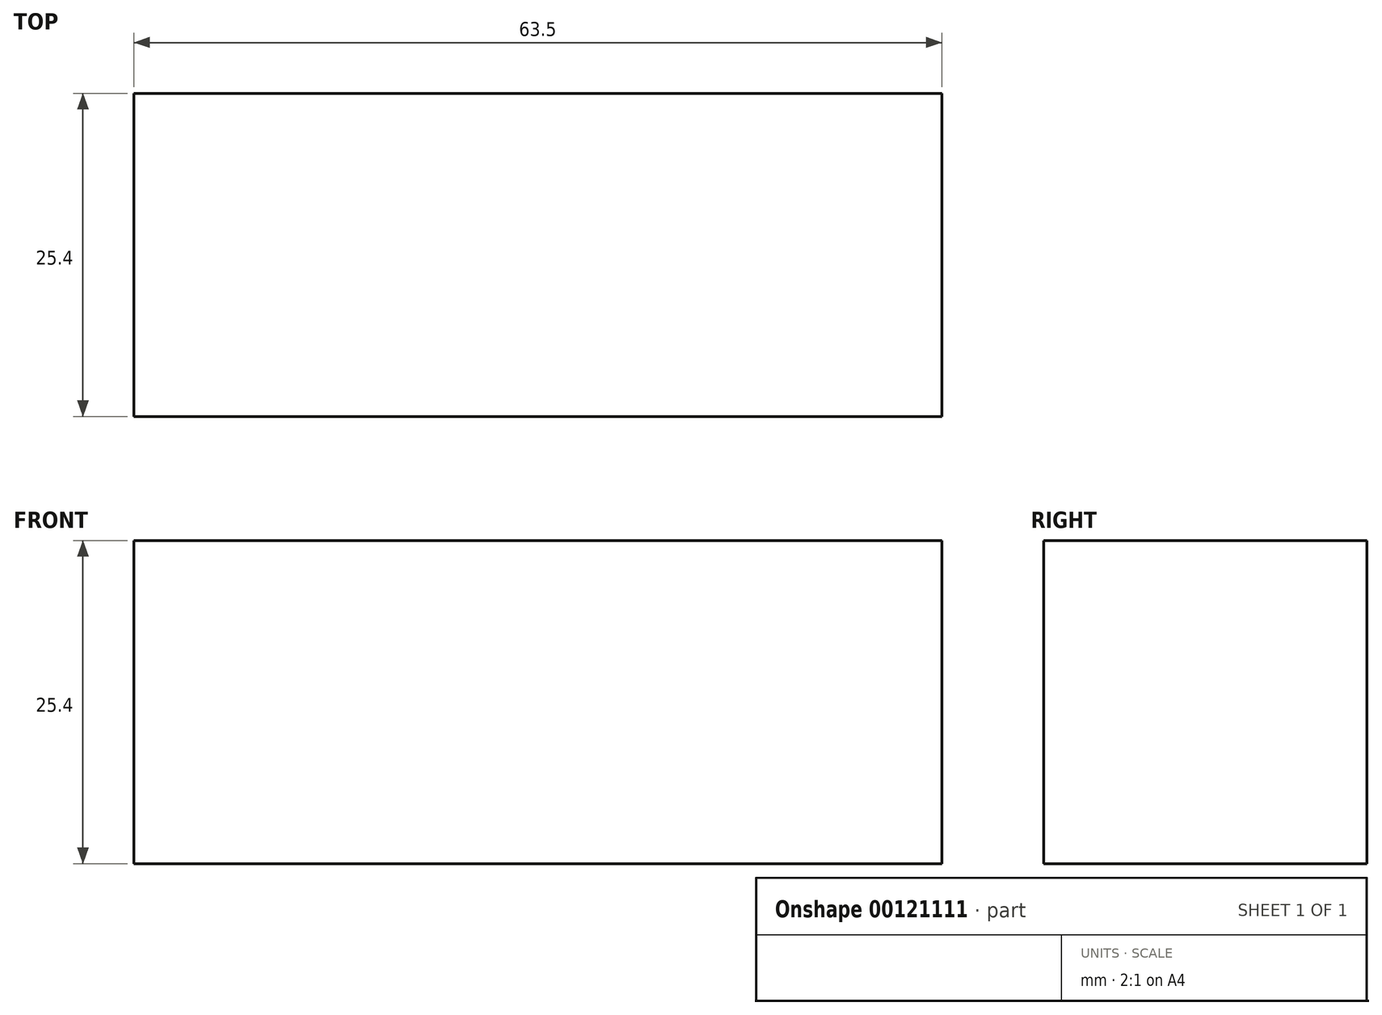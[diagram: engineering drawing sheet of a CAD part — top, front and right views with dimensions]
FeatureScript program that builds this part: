
annotation { "Feature Type Name" : "Feature", "Feature Type Description" : "" }
export const myFeature = defineFeature(function(context is Context, id is Id, definition is map)
    precondition{}
    {
        {
            var Q0;
            Q0=qCreatedBy(makeId("Front.planeOp"),FACE);
            var sketch = newSketch(context, id + "F0", { "sketchPlane" : qUnion([Q0])});
            skLineSegment(sketch, "E0.bottom", {"start": v(31.75, -12.7) * mm, "end": v(-31.75, -12.7) * mm});
            skLineSegment(sketch, "E0.top", {"start": v(31.75, 12.7) * mm, "end": v(-31.75, 12.7) * mm});
            skLineSegment(sketch, "E0.left", {"start": v(31.75, -12.7) * mm, "end": v(31.75, 12.7) * mm});
            skLineSegment(sketch, "E0.right", {"start": v(-31.75, -12.7) * mm, "end": v(-31.75, 12.7) * mm});
            skPoint(sketch, "E0.middle", {"position": v(0, 0) * mm});
            skLineSegment(sketch, "E1.bottom", {"start": v(84.18, 29.65) * mm, "end": v(46.08, 29.65) * mm});
            skLineSegment(sketch, "E1.top", {"start": v(84.18, 42.35) * mm, "end": v(46.08, 42.35) * mm});
            skLineSegment(sketch, "E1.left", {"start": v(84.18, 29.65) * mm, "end": v(84.18, 42.35) * mm});
            skLineSegment(sketch, "E1.right", {"start": v(46.08, 29.65) * mm, "end": v(46.08, 42.35) * mm});
            skPoint(sketch, "E1.middle", {"position": v(65.13, 36) * mm});
            skLineSegment(sketch, "E2", {"start": v(31.75, 12.7) * mm, "end": v(31.75, 23.77) * mm});
            skArc(sketch, "E3", {"start": v(31.75, 23.77) * mm, "mid": v(33.53, 28.05) * mm, "end": v(37.81, 29.82) * mm});
            skLineSegment(sketch, "E4", {"start": v(37.81, 29.82) * mm, "end": v(46.08, 29.65) * mm});
            skLineSegment(sketch, "E5.0", {"start": v(37.98, 42.52) * mm, "end": v(46.33, 42.35) * mm});
            skArc(sketch, "E5.1", {"start": v(19.05, 23.77) * mm, "mid": v(24.6, 37.1) * mm, "end": v(37.98, 42.52) * mm});
            skLineSegment(sketch, "E5.2", {"start": v(19.05, 12.7) * mm, "end": v(19.05, 23.77) * mm});
            skFitSpline(sketch, "E6", {"points": [v(-31.75, 12.7) * mm, v(31.7, 41.5) * mm, v(37.98, 42.52) * mm], "startDerivative": vector(103.96, 50.18) * mm, "endDerivative": vector(20.62, 0.6) * mm});
            skSolve(sketch);
        }
        {
            var Q0;
            Q0=makeQuery(id+"F0.imprint","IMPRINT",FACE,{"disambiguationData":[TD([[makeQuery(id+"F0.imprint","IMPRINT",EDGE,{"derivedFrom":sQuery(id+"F0.wireOp",EDGE,"E0.bottom")}),-1.0]])]});
            extrude(context, id + "F1", {"entities" : qUnion([Q0]), "endBound" : BoundingType.SYMMETRIC, "depth" : 25.4 * mm});
        }
    });
